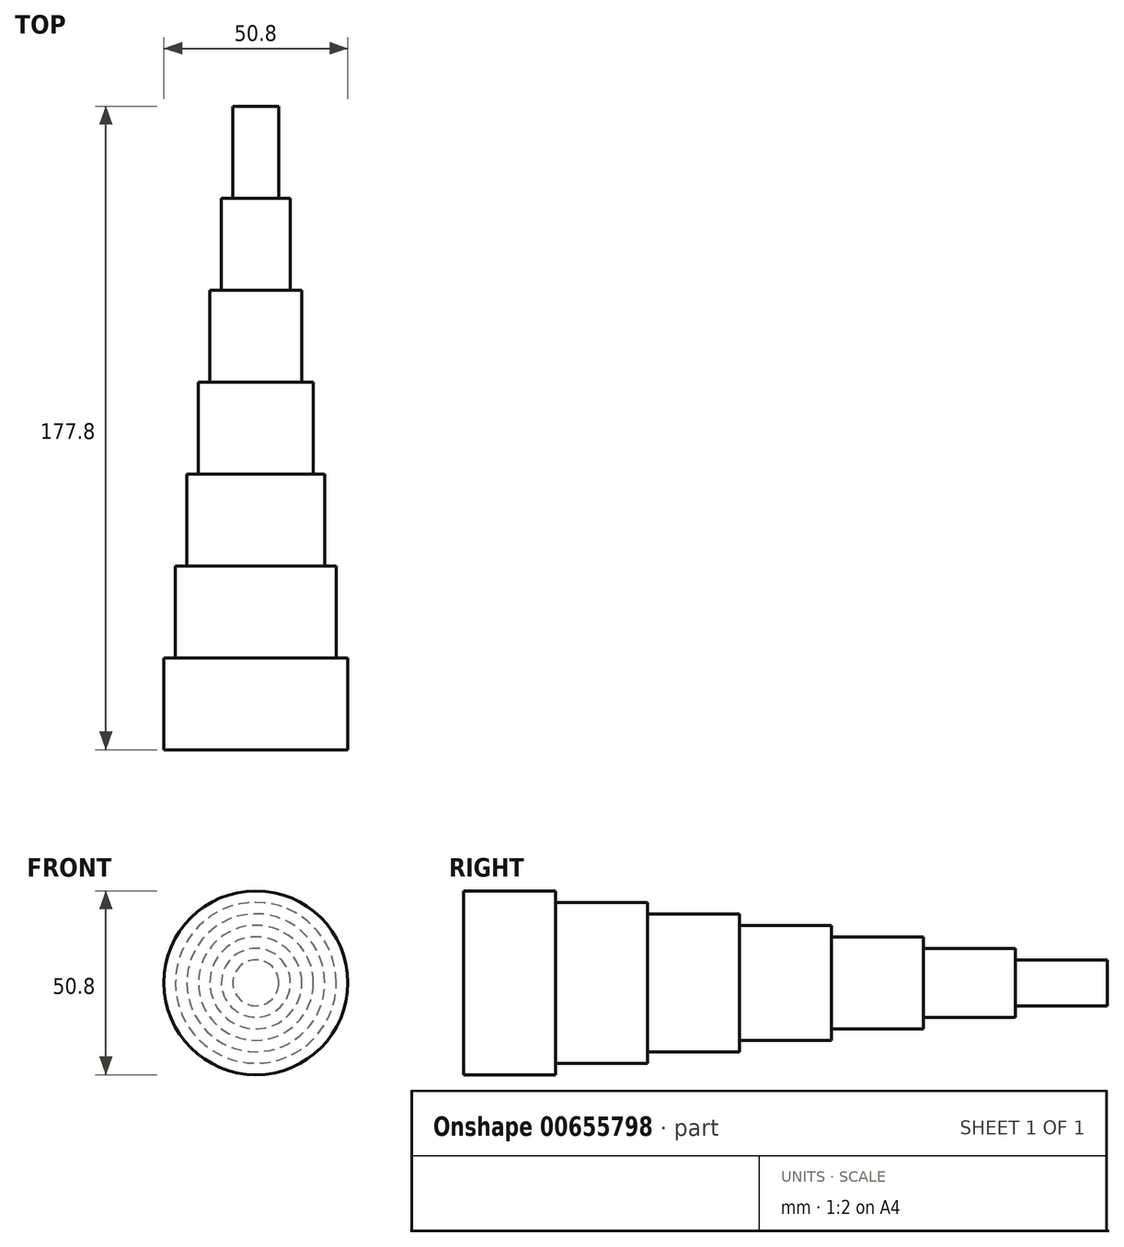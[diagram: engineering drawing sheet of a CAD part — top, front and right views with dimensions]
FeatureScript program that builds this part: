
annotation { "Feature Type Name" : "Feature", "Feature Type Description" : "" }
export const myFeature = defineFeature(function(context is Context, id is Id, definition is map)
    precondition{}
    {
        {
            var Q0;
            Q0=qCreatedBy(makeId("Front.planeOp"),FACE);
            var sketch = newSketch(context, id + "F0", { "sketchPlane" : qUnion([Q0])});
            skCircle(sketch, "E0", {"center": v(0, 0) * mm, "radius": 6.35 * mm});
            skSolve(sketch);
        }
        {
            var Q0;
            Q0 = qSketchRegion(id + "F0", true);
            extrude(context, id + "F1", {"entities" : qUnion([Q0]), "depth" : 25.4 * mm, "offsetDistance" : 25.4 * mm});
        }
        {
            var Q0;
            Q0=makeQuery(id+"F1.opExtrude","CAP_FACE",FACE,{"disambiguationData":[OSD([sQuery(id+"F0.wireOp",EDGE,"E0")])],"isStart":false});
            var sketch = newSketch(context, id + "F2", { "sketchPlane" : qUnion([Q0])});
            skCircle(sketch, "E1", {"center": v(0, 0) * mm, "radius": 9.53 * mm});
            skSolve(sketch);
        }
        {
            var Q0;
            Q0 = qSketchRegion(id + "F2", true);
            extrude(context, id + "F3", {"entities" : qUnion([Q0]), "operationType" : NewBodyOperationType.ADD, "depth" : 25.4 * mm, "offsetDistance" : 25.4 * mm});
        }
        {
            var Q0;
            Q0=makeQuery(id+"F3.opExtrude","CAP_FACE",FACE,{"disambiguationData":[OSD([sQuery(id+"F2.wireOp",EDGE,"E1")])],"isStart":false});
            var sketch = newSketch(context, id + "F4", { "sketchPlane" : qUnion([Q0])});
            skCircle(sketch, "E2", {"center": v(0, 0) * mm, "radius": 12.7 * mm});
            skSolve(sketch);
        }
        {
            var Q0;
            Q0 = qSketchRegion(id + "F4", true);
            extrude(context, id + "F5", {"entities" : qUnion([Q0]), "operationType" : NewBodyOperationType.ADD, "depth" : 25.4 * mm, "offsetDistance" : 25.4 * mm});
        }
        {
            var Q0;
            Q0=makeQuery(id+"F5.opExtrude","CAP_FACE",FACE,{"disambiguationData":[OSD([sQuery(id+"F4.wireOp",EDGE,"E2")])],"isStart":false});
            var sketch = newSketch(context, id + "F6", { "sketchPlane" : qUnion([Q0])});
            skCircle(sketch, "E3", {"center": v(0, 0) * mm, "radius": 15.88 * mm});
            skSolve(sketch);
        }
        {
            var Q0;
            Q0 = qSketchRegion(id + "F6", true);
            extrude(context, id + "F7", {"entities" : qUnion([Q0]), "operationType" : NewBodyOperationType.ADD, "depth" : 25.4 * mm, "offsetDistance" : 25.4 * mm});
        }
        {
            var Q0;
            Q0=makeQuery(id+"F7.opExtrude","CAP_FACE",FACE,{"disambiguationData":[OSD([sQuery(id+"F6.wireOp",EDGE,"E3")])],"isStart":false});
            var sketch = newSketch(context, id + "F8", { "sketchPlane" : qUnion([Q0])});
            skCircle(sketch, "E4", {"center": v(0, 0) * mm, "radius": 19.05 * mm});
            skSolve(sketch);
        }
        {
            var Q0;
            Q0 = qSketchRegion(id + "F8", true);
            extrude(context, id + "F9", {"entities" : qUnion([Q0]), "operationType" : NewBodyOperationType.ADD, "depth" : 25.4 * mm, "offsetDistance" : 25.4 * mm});
        }
        {
            var Q0;
            Q0=makeQuery(id+"F9.opExtrude","CAP_FACE",FACE,{"disambiguationData":[OSD([sQuery(id+"F8.wireOp",EDGE,"E4")])],"isStart":false});
            var sketch = newSketch(context, id + "F10", { "sketchPlane" : qUnion([Q0])});
            skCircle(sketch, "E5", {"center": v(0, 0) * mm, "radius": 22.23 * mm});
            skSolve(sketch);
        }
        {
            var Q0;
            Q0 = qSketchRegion(id + "F10", true);
            extrude(context, id + "F11", {"entities" : qUnion([Q0]), "operationType" : NewBodyOperationType.ADD, "depth" : 25.4 * mm, "offsetDistance" : 25.4 * mm});
        }
        {
            var Q0;
            Q0=makeQuery(id+"F11.opExtrude","CAP_FACE",FACE,{"disambiguationData":[OSD([sQuery(id+"F10.wireOp",EDGE,"E5")])],"isStart":false});
            var sketch = newSketch(context, id + "F12", { "sketchPlane" : qUnion([Q0])});
            skCircle(sketch, "E6", {"center": v(0, 0) * mm, "radius": 25.4 * mm});
            skSolve(sketch);
        }
        {
            var Q0;
            Q0 = qSketchRegion(id + "F12", true);
            extrude(context, id + "F13", {"entities" : qUnion([Q0]), "operationType" : NewBodyOperationType.ADD, "depth" : 25.4 * mm, "offsetDistance" : 25.4 * mm});
        }
    });
